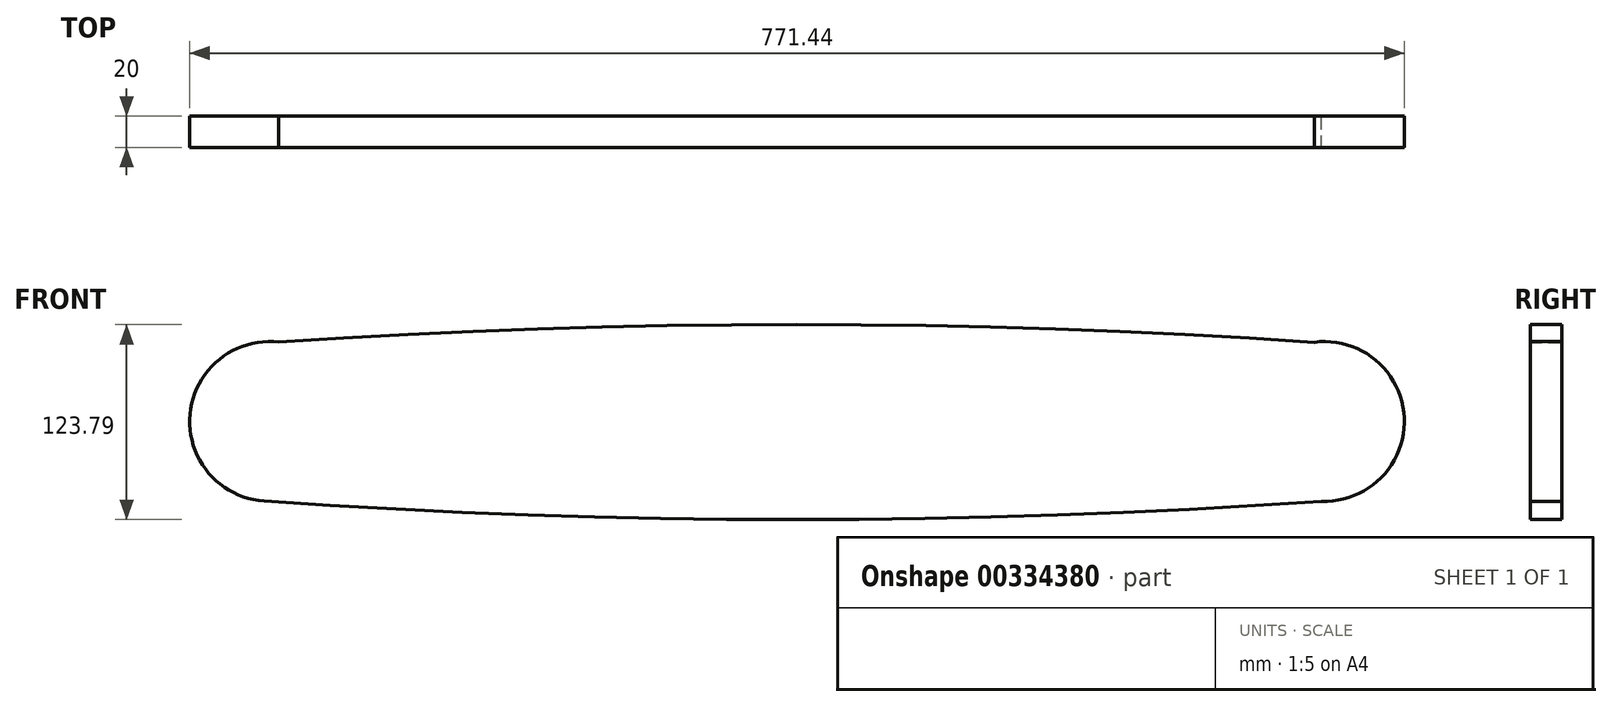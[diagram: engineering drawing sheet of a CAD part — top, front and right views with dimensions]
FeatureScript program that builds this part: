
annotation { "Feature Type Name" : "Feature", "Feature Type Description" : "" }
export const myFeature = defineFeature(function(context is Context, id is Id, definition is map)
    precondition{}
    {
        {
            var Q0;
            Q0=qCreatedBy(makeId("Front.planeOp"),FACE);
            var sketch = newSketch(context, id + "F0", { "sketchPlane" : qUnion([Q0])});
            skCircle(sketch, "E0", {"center": v(-51.58, 0) * mm, "radius": 50.72 * mm});
            skCircle(sketch, "E1", {"center": v(618.42, 0) * mm, "radius": 50.72 * mm});
            skLineSegment(sketch, "E2", {"start": v(-51.58, 0) * mm, "end": v(618.42, 0) * mm});
            skArc(sketch, "E3", {"start": v(-55.1, -50.6) * mm, "mid": v(280.74, -62.29) * mm, "end": v(616.59, -50.69) * mm});
            skArc(sketch, "E4", {"start": v(611.89, 50.3) * mm, "mid": v(283.1, 61.5) * mm, "end": v(-45.7, 50.38) * mm});
            skSolve(sketch);
        }
        {
            var Q0;
            {var subQ0=sQuery(id+"F0.wireOp",EDGE,"E4");Q0=makeQuery(id+"F0.imprint","IMPRINT",FACE,{"disambiguationData":[TD([[makeQuery(id+"F0.imprint","IMPRINT",EDGE,{"derivedFrom":subQ0}),1.0]])]});}
            var Q1;
            {var subQ0=sQuery(id+"F0.wireOp",EDGE,"E0");var subQ1=makeQuery(id+"F0.imprint","INTERSECT",VERTEX,{"derivedFrom":[subQ0,sQuery(id+"F0.wireOp",EDGE,"E4")]});Q1=makeQuery(id+"F0.imprint","IMPRINT",FACE,{"disambiguationData":[TD([[makeQuery(id+"F0.imprint","IMPRINT",EDGE,{"disambiguationData":[TD([[subQ1,1.0]])],"derivedFrom":subQ0}),1.0]])]});}
            var Q2;
            {var subQ0=sQuery(id+"F0.wireOp",EDGE,"E3");Q2=makeQuery(id+"F0.imprint","IMPRINT",FACE,{"disambiguationData":[TD([[makeQuery(id+"F0.imprint","IMPRINT",EDGE,{"derivedFrom":subQ0}),1.0]])]});}
            var Q3;
            {var subQ0=sQuery(id+"F0.wireOp",EDGE,"E1");var subQ1=makeQuery(id+"F0.imprint","INTERSECT",VERTEX,{"derivedFrom":[subQ0,sQuery(id+"F0.wireOp",EDGE,"E4")]});Q3=makeQuery(id+"F0.imprint","IMPRINT",FACE,{"disambiguationData":[TD([[makeQuery(id+"F0.imprint","IMPRINT",EDGE,{"disambiguationData":[TD([[subQ1,-1.0]])],"derivedFrom":subQ0}),1.0]])]});}
            extrude(context, id + "F1", {"entities" : qUnion([Q0, Q1, Q2, Q3]), "depth" : 20 * mm});
        }
    });
